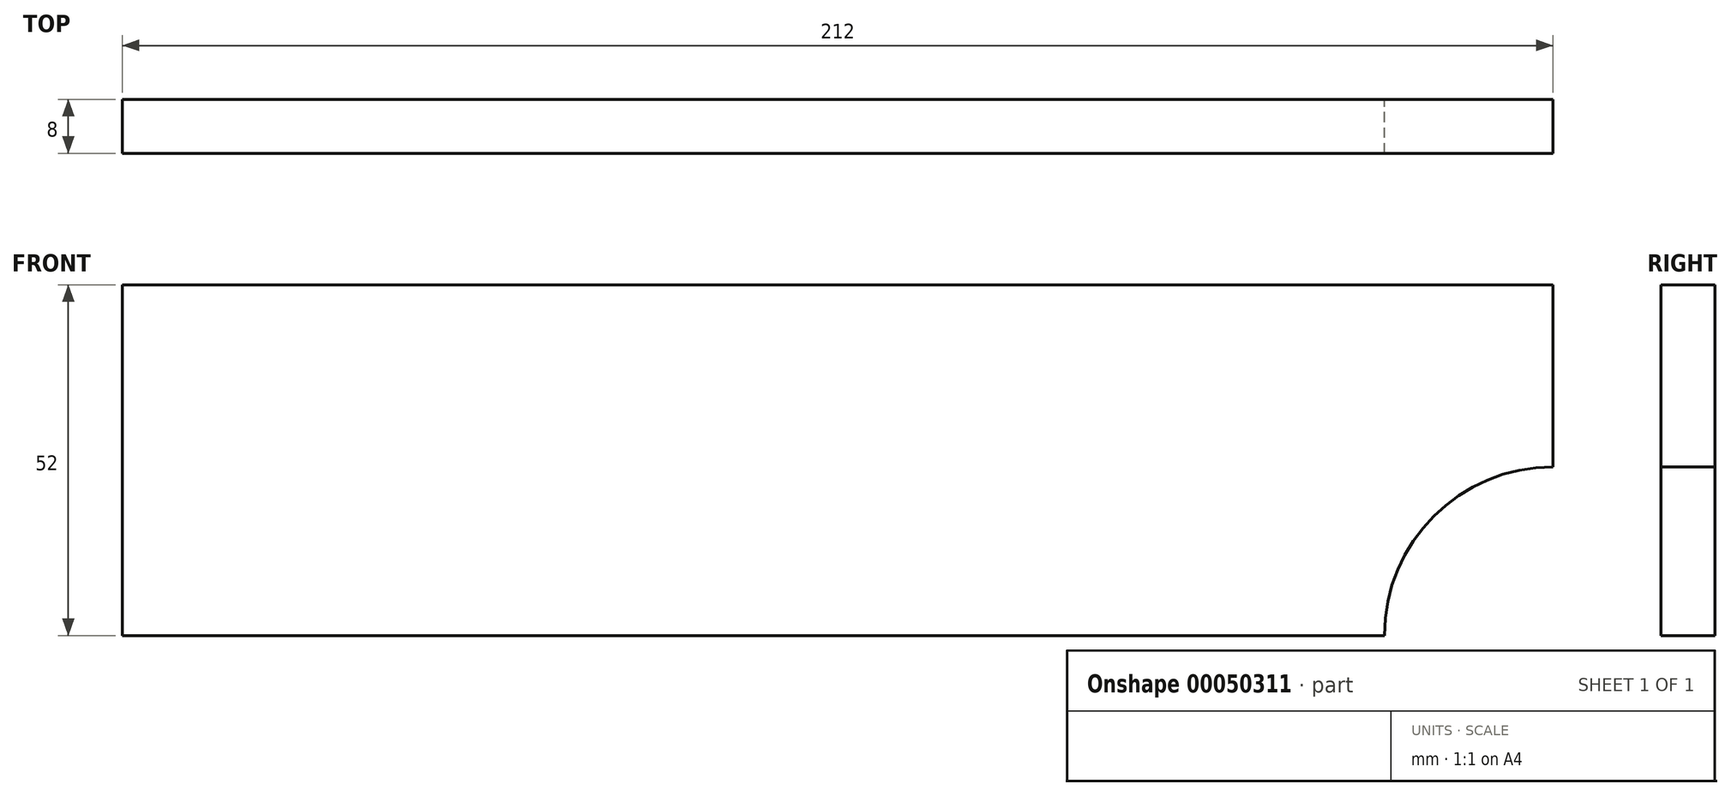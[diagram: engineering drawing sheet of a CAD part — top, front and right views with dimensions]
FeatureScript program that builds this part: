
annotation { "Feature Type Name" : "Feature", "Feature Type Description" : "" }
export const myFeature = defineFeature(function(context is Context, id is Id, definition is map)
    precondition{}
    {
        {
            var Q0;
            Q0=qCreatedBy(makeId("Front.planeOp"),FACE);
            var sketch = newSketch(context, id + "F0", { "sketchPlane" : qUnion([Q0])});
            skLineSegment(sketch, "E0.bottom", {"start": v(0, 0) * mm, "end": v(-212, 0) * mm});
            skLineSegment(sketch, "E0.top", {"start": v(-25, -52) * mm, "end": v(-212, -52) * mm});
            skLineSegment(sketch, "E0.left", {"start": v(0, 0) * mm, "end": v(0, -27) * mm});
            skLineSegment(sketch, "E0.right", {"start": v(-212, 0) * mm, "end": v(-212, -52) * mm});
            skArc(sketch, "E1", {"start": v(0, -27) * mm, "mid": v(-17.68, -34.32) * mm, "end": v(-25, -52) * mm});
            skPoint(sketch, "E2", {"position": v(0, -27) * mm});
            skPoint(sketch, "E3", {"position": v(-25, -52) * mm});
            skSolve(sketch);
        }
        {
            var Q0;
            Q0=qSketchRegion(id+"F0",true);
            extrude(context, id + "F1", {"entities" : qUnion([Q0]), "depth" : 8 * mm});
        }
    });
